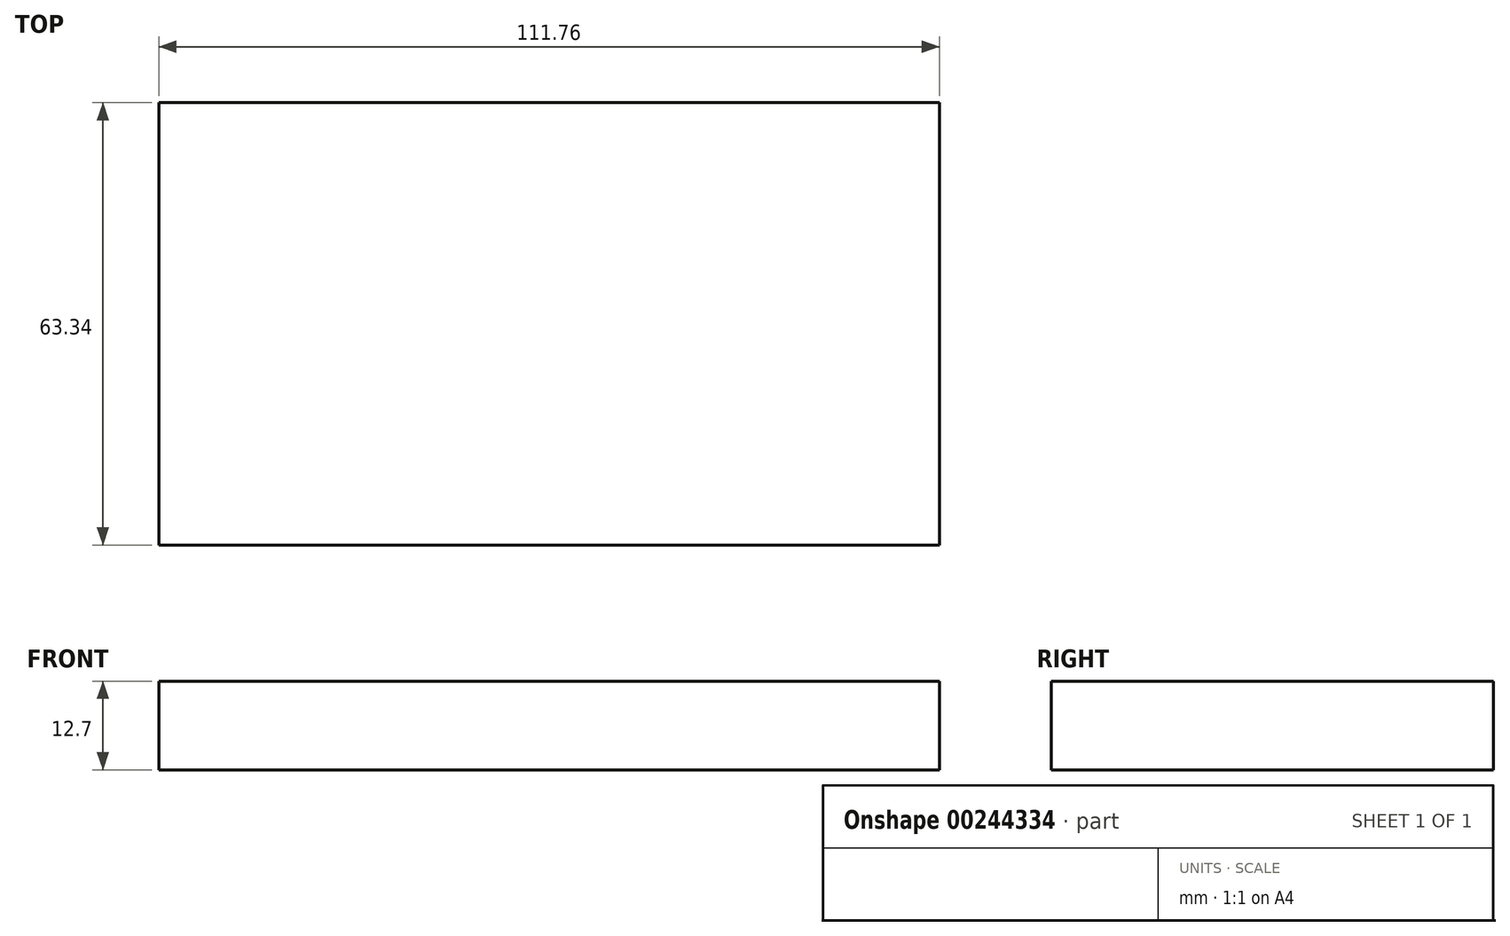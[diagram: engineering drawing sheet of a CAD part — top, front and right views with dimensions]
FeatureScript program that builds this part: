
annotation { "Feature Type Name" : "Feature", "Feature Type Description" : "" }
export const myFeature = defineFeature(function(context is Context, id is Id, definition is map)
    precondition{}
    {
        {
            var Q0;
            Q0=qCreatedBy(makeId("Top.planeOp"),FACE);
            var sketch = newSketch(context, id + "F0", { "sketchPlane" : qUnion([Q0])});
            skLineSegment(sketch, "E0.bottom", {"start": v(-55.88, 31.67) * mm, "end": v(55.88, 31.67) * mm});
            skLineSegment(sketch, "E0.top", {"start": v(-55.88, -31.67) * mm, "end": v(55.88, -31.67) * mm});
            skLineSegment(sketch, "E0.left", {"start": v(-55.88, 31.67) * mm, "end": v(-55.88, -31.67) * mm});
            skLineSegment(sketch, "E0.right", {"start": v(55.88, 31.67) * mm, "end": v(55.88, -31.67) * mm});
            skPoint(sketch, "E0.middle", {"position": v(0, 0) * mm});
            skSolve(sketch);
        }
        {
            var Q0;
            Q0 = qSketchRegion(id + "F0", true);
            extrude(context, id + "F1", {"entities" : qUnion([Q0]), "oppositeDirection" : true, "depth" : 12.7 * mm});
        }
    });
